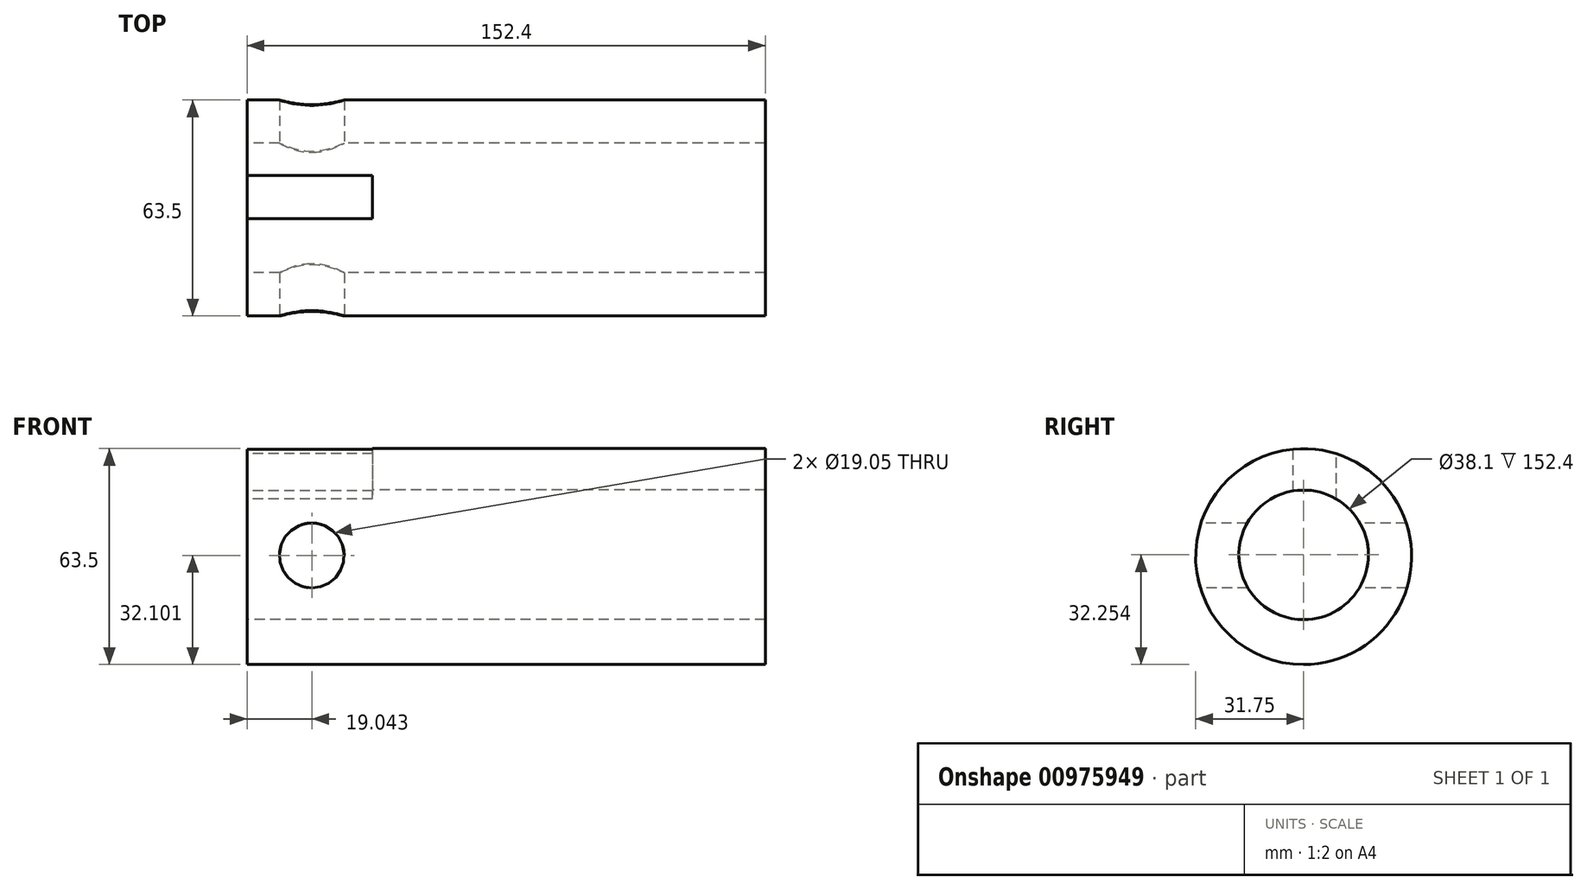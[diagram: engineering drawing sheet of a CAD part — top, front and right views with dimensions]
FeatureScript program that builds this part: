
annotation { "Feature Type Name" : "Feature", "Feature Type Description" : "" }
export const myFeature = defineFeature(function(context is Context, id is Id, definition is map)
    precondition{}
    {
        {
            var Q0;
            Q0=qCreatedBy(makeId("Right.planeOp"),FACE);
            var sketch = newSketch(context, id + "F0", { "sketchPlane" : qUnion([Q0])});
            skCircle(sketch, "E0", {"center": v(0.2, -0.06) * mm, "radius": 31.75 * mm});
            skSolve(sketch);
        }
        {
            var Q0;
            Q0=qCreatedBy(makeId("Right.planeOp"),FACE);
            var sketch = newSketch(context, id + "F1", { "sketchPlane" : qUnion([Q0])});
            skCircle(sketch, "E1", {"center": v(0.2, 0.44) * mm, "radius": 19.05 * mm});
            skSolve(sketch);
        }
        {
            var Q0;
            Q0=makeQuery(id+"F0.imprint","IMPRINT",FACE,{"disambiguationData":[TD([[makeQuery(id+"F0.imprint","IMPRINT",EDGE,{"derivedFrom":sQuery(id+"F0.wireOp",EDGE,"E0")}),1.0]])]});
            extrude(context, id + "F2", {"entities" : qUnion([Q0]), "depth" : 152.4 * mm, "offsetDistance" : 25.4 * mm});
        }
        {
            var Q0;
            Q0=makeQuery(id+"F1.imprint","IMPRINT",FACE,{"disambiguationData":[TD([[makeQuery(id+"F1.imprint","IMPRINT",EDGE,{"derivedFrom":sQuery(id+"F1.wireOp",EDGE,"E1")}),1.0]])]});
            extrude(context, id + "F3", {"entities" : qUnion([Q0]), "operationType" : NewBodyOperationType.REMOVE, "depth" : 152.4 * mm, "offsetDistance" : 25.4 * mm});
        }
        {
            var Q0;
            Q0=qCreatedBy(makeId("Front.planeOp"),FACE);
            var sketch = newSketch(context, id + "F4", { "sketchPlane" : qUnion([Q0])});
            skCircle(sketch, "E2", {"center": v(19.04, 0.3) * mm, "radius": 9.53 * mm});
            skSolve(sketch);
        }
        {
            var Q0;
            Q0 = qSketchRegion(id + "F4", true);
            extrude(context, id + "F5", {"entities" : qUnion([Q0]), "operationType" : NewBodyOperationType.REMOVE, "oppositeDirection" : true, "depth" : 76.2 * mm, "offsetDistance" : 25.4 * mm, "symmetric" : true});
        }
        {
            var Q0;
            Q0=qCreatedBy(makeId("Top.planeOp"),FACE);
            var sketch = newSketch(context, id + "F6", { "sketchPlane" : qUnion([Q0])});
            skLineSegment(sketch, "E3.bottom", {"start": v(-1.19, 9.81) * mm, "end": v(36.91, 9.81) * mm});
            skLineSegment(sketch, "E3.top", {"start": v(-1.19, -2.89) * mm, "end": v(36.91, -2.89) * mm});
            skLineSegment(sketch, "E3.left", {"start": v(-1.19, 9.81) * mm, "end": v(-1.19, -2.89) * mm});
            skLineSegment(sketch, "E3.right", {"start": v(36.91, 9.81) * mm, "end": v(36.91, -2.89) * mm});
            skSolve(sketch);
        }
        {
            var Q0;
            Q0 = qSketchRegion(id + "F6", true);
            extrude(context, id + "F7", {"entities" : qUnion([Q0]), "operationType" : NewBodyOperationType.REMOVE, "oppositeDirection" : true, "depth" : -50.8 * mm, "offsetDistance" : 25.4 * mm});
        }
    });
